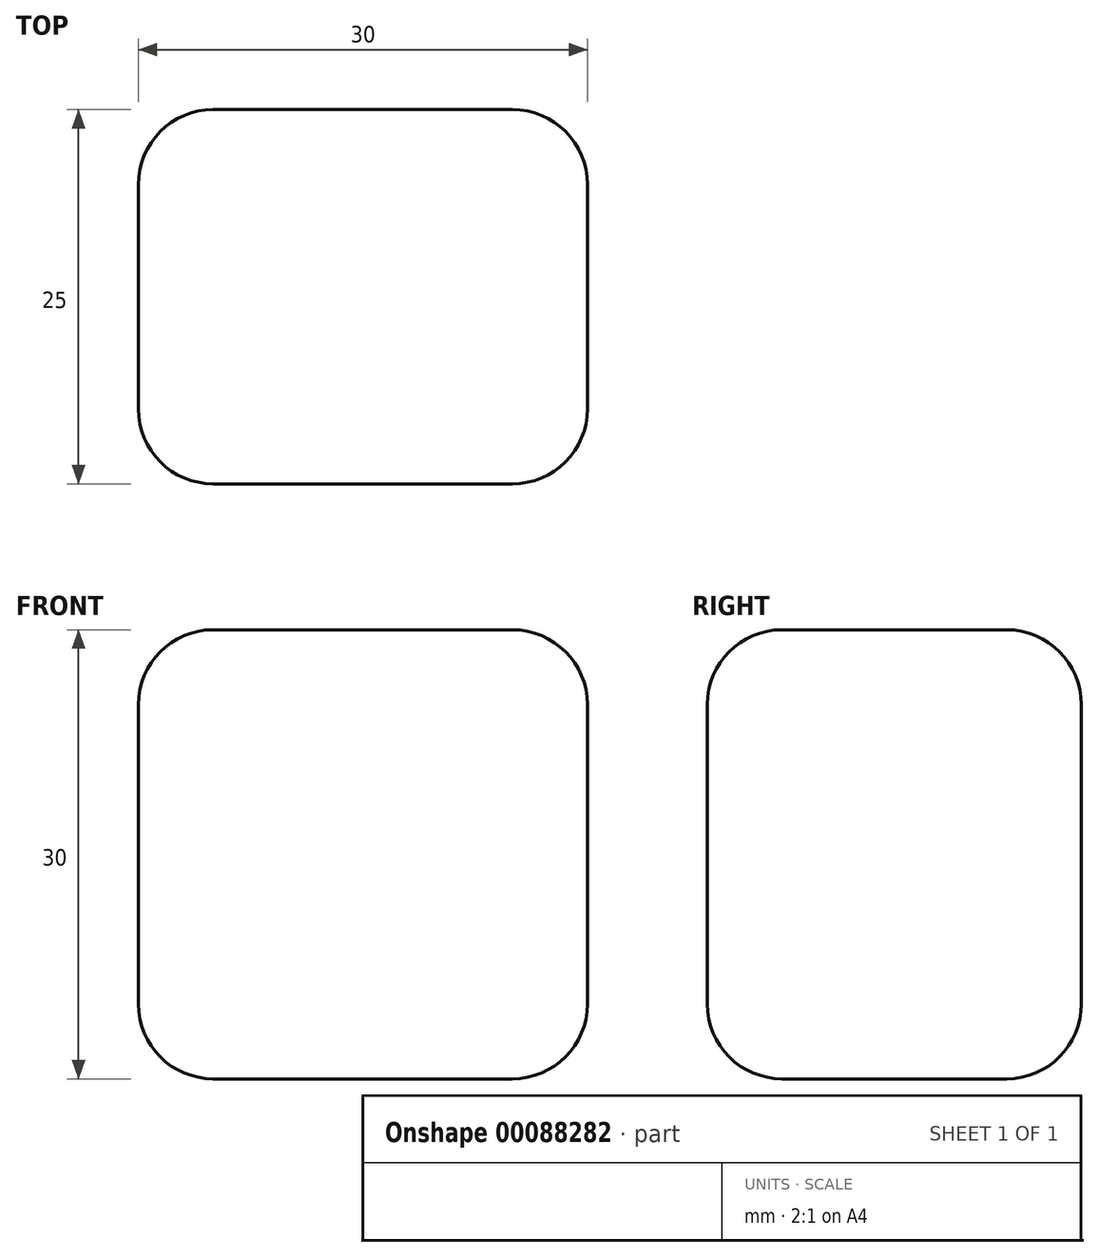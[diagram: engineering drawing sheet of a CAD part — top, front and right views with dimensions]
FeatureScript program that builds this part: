
annotation { "Feature Type Name" : "Feature", "Feature Type Description" : "" }
export const myFeature = defineFeature(function(context is Context, id is Id, definition is map)
    precondition{}
    {
        {
            var Q0;
            Q0=qCreatedBy(makeId("Front.planeOp"),FACE);
            var sketch = newSketch(context, id + "F0", { "sketchPlane" : qUnion([Q0])});
            skLineSegment(sketch, "E0.bottom", {"start": v(-49.31, 23.65) * mm, "end": v(-19.31, 23.65) * mm});
            skLineSegment(sketch, "E0.top", {"start": v(-49.31, 53.65) * mm, "end": v(-19.31, 53.65) * mm});
            skLineSegment(sketch, "E0.left", {"start": v(-49.31, 23.65) * mm, "end": v(-49.31, 53.65) * mm});
            skLineSegment(sketch, "E0.right", {"start": v(-19.31, 23.65) * mm, "end": v(-19.31, 53.65) * mm});
            skSolve(sketch);
        }
        {
            var Q0;
            Q0=makeQuery(id+"F0.imprint","IMPRINT",FACE,{"disambiguationData":[TD([[makeQuery(id+"F0.imprint","IMPRINT",EDGE,{"derivedFrom":sQuery(id+"F0.wireOp",EDGE,"E0.bottom")}),1.0]])]});
            extrude(context, id + "F1", {"entities" : qUnion([Q0]), "depth" : 25 * mm});
        }
        {
            var Q0;
            Q0=makeQuery(id+"F1.opExtrude","CAP_EDGE",EDGE,{"disambiguationData":[OSD([sQuery(id+"F0.wireOp",EDGE,"E0.left")])],"isStart":false});
            var Q1;
            Q1=makeQuery(id+"F1.opExtrude","SWEPT_EDGE",EDGE,{"disambiguationData":[OSD([sQuery(id+"F0.wireOp",EDGE,"E0.top"),sQuery(id+"F0.wireOp",EDGE,"E0.left")])]});
            var Q2;
            Q2=makeQuery(id+"F1.opExtrude","CAP_EDGE",EDGE,{"disambiguationData":[OSD([sQuery(id+"F0.wireOp",EDGE,"E0.top")])],"isStart":false});
            var Q3;
            Q3=makeQuery(id+"F1.opExtrude","CAP_EDGE",EDGE,{"disambiguationData":[OSD([sQuery(id+"F0.wireOp",EDGE,"E0.right")])],"isStart":false});
            var Q4;
            Q4=makeQuery(id+"F1.opExtrude","CAP_EDGE",EDGE,{"disambiguationData":[OSD([sQuery(id+"F0.wireOp",EDGE,"E0.bottom")])],"isStart":false});
            var Q5;
            Q5=makeQuery(id+"F1.opExtrude","SWEPT_EDGE",EDGE,{"disambiguationData":[OSD([sQuery(id+"F0.wireOp",EDGE,"E0.bottom"),sQuery(id+"F0.wireOp",EDGE,"E0.left")])]});
            var Q6;
            Q6=makeQuery(id+"F1.opExtrude","CAP_EDGE",EDGE,{"disambiguationData":[OSD([sQuery(id+"F0.wireOp",EDGE,"E0.left")])],"isStart":true});
            var Q7;
            Q7=makeQuery(id+"F1.opExtrude","CAP_EDGE",EDGE,{"disambiguationData":[OSD([sQuery(id+"F0.wireOp",EDGE,"E0.bottom")])],"isStart":true});
            var Q8;
            Q8=makeQuery(id+"F1.opExtrude","SWEPT_EDGE",EDGE,{"disambiguationData":[OSD([sQuery(id+"F0.wireOp",EDGE,"E0.top"),sQuery(id+"F0.wireOp",EDGE,"E0.right")])]});
            var Q9;
            Q9=makeQuery(id+"F1.opExtrude","SWEPT_EDGE",EDGE,{"disambiguationData":[OSD([sQuery(id+"F0.wireOp",EDGE,"E0.bottom"),sQuery(id+"F0.wireOp",EDGE,"E0.right")])]});
            var Q10;
            Q10=makeQuery(id+"F1.opExtrude","CAP_EDGE",EDGE,{"disambiguationData":[OSD([sQuery(id+"F0.wireOp",EDGE,"E0.top")])],"isStart":true});
            var Q11;
            Q11=makeQuery(id+"F1.opExtrude","CAP_EDGE",EDGE,{"disambiguationData":[OSD([sQuery(id+"F0.wireOp",EDGE,"E0.right")])],"isStart":true});
            fillet(context, id + "F2", {"entities" : qUnion([Q0, Q1, Q2, Q3, Q4, Q5, Q6, Q7, Q8, Q9, Q10, Q11]), "radius" : 5 * mm, "tangentPropagation" : true, "allowEdgeOverflow" : false});
        }
    });
